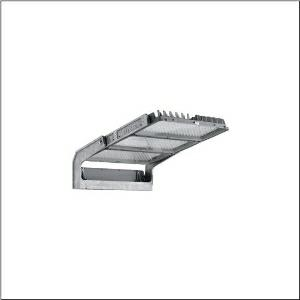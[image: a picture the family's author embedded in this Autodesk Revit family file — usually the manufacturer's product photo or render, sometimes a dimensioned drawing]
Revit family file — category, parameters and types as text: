
# Revit family: floodlight_fl_11_maxi_pro___rs08_5xa779129l02fb_e772
name_source: partatom
category: Lighting Fixtures
units: mm (PartAtom-declared; Revit-internal decimal feet)

## family parameters
Cut with Voids When Loaded = No
Host = Face
Light Source = No
Part Type = Normal
Room Calculation Point = No
Round Connector Dimension = Use Diameter
Shared = No

## types (1)
- --- (1 x LED, 171610 lm, 1400 W, 5700K)
    Apparent Load = 1400 VA
    CIE Flux Codes = 70 87 98 100 100
    Color Rendering = 70
    Color Temperature = 5700K
    Default Elevation = 1800 mm
    Description = Floodlight FL 11  maxi  pro floodlight; light control with lens of PMMA; cover panel of toughened safety glass, transparent; light distribution: RS08, rotationally symmetric direct distribution, LEDcolour temperature: 5700K, rated luminous flux: 171.610lm, colour rendering: CRI > 70, light colour: 757; luminous efficacy: 123lm/W; brightness control: DALI 2; with terminal, 5-pole, max. 2.5mm², mains connection: 220..240V/380..400V AC, 50/60Hz, surge voltage resistance: line to ground: 10kV, service life up to 100,000h L90. Typical operating time: 1000h per year, ECG replaceable separately, LED unit replaceable without ESD environment, dustproof LED module, dimming range 10..100%; 1400W floodlight with 3x LED unit of diecast aluminium, coated grey; length: 1.003mm / width: 651mm / height: 338mm; mounting bracket, of diecast aluminium, uncoated, natural, protection rating (complete): IP66; insulation class (complete): insulation class I (protective earthing); certification: CE, ENEC, VDE; ball protection: ball impact resistant, only for outdoor installations in the designated locations, permissible operating ambient temperature: -45..+55°C, permissible storage temperature: -40..+85°Cpackaging unit: 1 piece

Light Distribution: RS08
    Height = 320 mm
    Lamp = 1 x LED
    Lamp Light Flux = 171610 lm
    Lamp Power = 1400 W
    Lamp count = 1
    Length = 1002 mm
    Luminous efficacy = 123 lm/W
    Manufacturer = Siteco
    ModVariant = No
    Model = 5XA779129L02FB
    Mounting Place = Ceiling
    Mounting Type = Surface mounted
    Number of Poles = 1
    OnlyDefault = Yes
    Power Factor = 1
    Product Name = Floodlight FL 11 maxi pro | RS08
    Product group = floodlight | ceiling mounted
    ProductGroupID = 301
    Protection Class = Protection class I
    Protection Degree = IP 66
    RLX_Detail_Level = 1
    RLX_Emergency_Light_Flux = 0 lm
    RLX_Emergency_Type = 0
    RLX_Emergency_Type_DB = No
    RlxData = <blob elided: 40369 chars, md5=7efc7771>
    Socket = socket
    Standby Power = 0 W
    System Light Flux = 171610 lm
    System Power = 1400 W
    Type Comments = factory setting: luminous flux: 100 % | dim-lin: 254 | 955 mA
    Type Image = l_1356210.jpg
    URL = http://relux.com
    VarID = @adj_024802
    Voltage = 0 V
    Weight = 0.00 kg
    Width = 655 mm

## geometry (parser evidence)
native form markers: Blend x4, Sweep x10
no freeform markers — native parametric forms only
